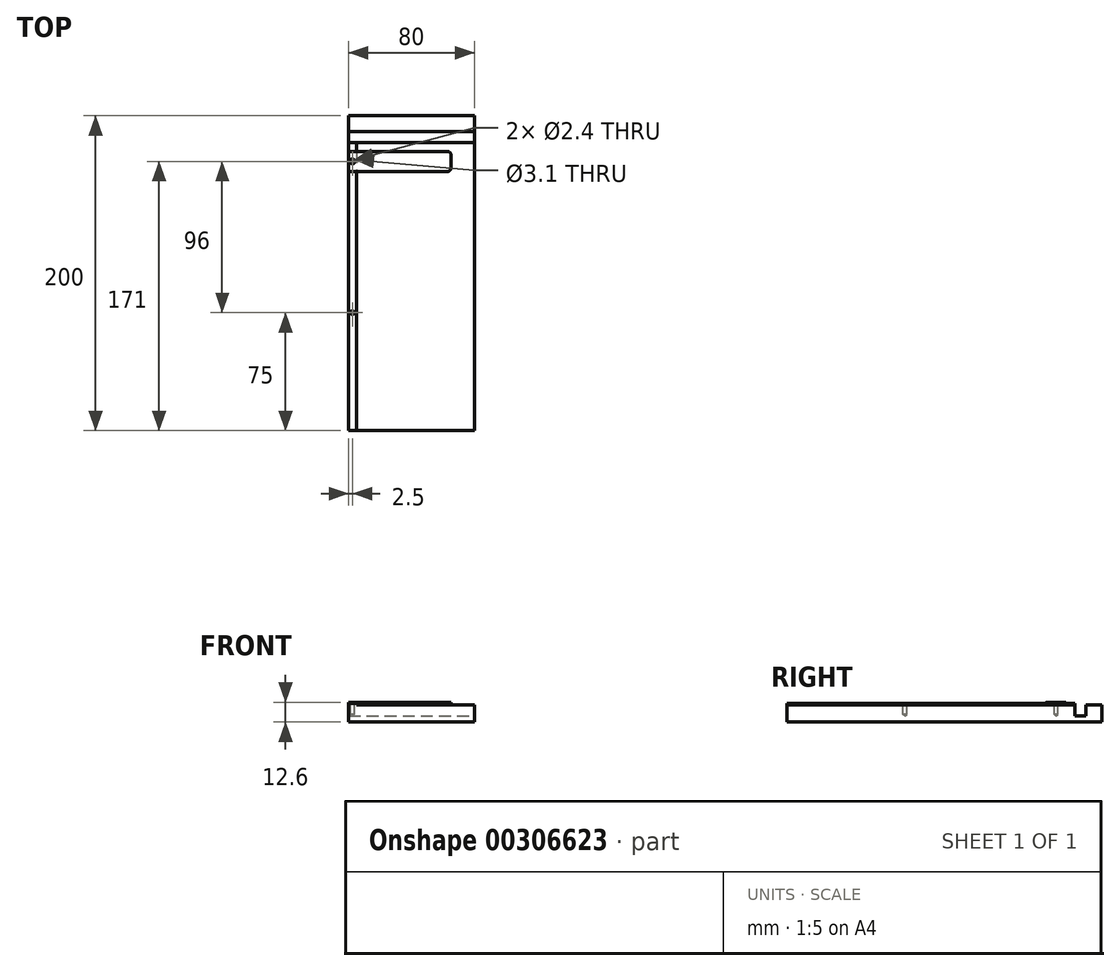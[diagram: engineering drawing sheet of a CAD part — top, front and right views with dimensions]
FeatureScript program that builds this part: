
annotation { "Feature Type Name" : "Feature", "Feature Type Description" : "" }
export const myFeature = defineFeature(function(context is Context, id is Id, definition is map)
    precondition{}
    {
        {
            var Q0;
            Q0=qCreatedBy(makeId("Right.planeOp"),FACE);
            var sketch = newSketch(context, id + "F0", { "sketchPlane" : qUnion([Q0])});
            skLineSegment(sketch, "E0", {"start": v(0, 0) * mm, "end": v(183, 0) * mm});
            skLineSegment(sketch, "E1", {"start": v(183, 0) * mm, "end": v(183, -7) * mm});
            skLineSegment(sketch, "E2", {"start": v(183, -7) * mm, "end": v(190, -7) * mm});
            skLineSegment(sketch, "E3", {"start": v(190, -7) * mm, "end": v(190, 0) * mm});
            skLineSegment(sketch, "E4", {"start": v(190, 0) * mm, "end": v(200, 0) * mm});
            skLineSegment(sketch, "E5", {"start": v(200, 0) * mm, "end": v(200, -11) * mm});
            skLineSegment(sketch, "E6", {"start": v(200, -11) * mm, "end": v(0, -11) * mm});
            skLineSegment(sketch, "E7", {"start": v(0, -11) * mm, "end": v(0, 0) * mm});
            skSolve(sketch);
        }
        {
            var Q0;
            Q0=qSketchRegion(id+"F0",true);
            extrude(context, id + "F1", {"entities" : qUnion([Q0]), "oppositeDirection" : true, "depth" : 80 * mm});
        }
        {
            var Q0;
            Q0=makeQuery(id+"F1.opExtrude","SWEPT_FACE",FACE,{"disambiguationData":[OSD([sQuery(id+"F0.wireOp",EDGE,"E0")])]});
            var sketch = newSketch(context, id + "F2", { "sketchPlane" : qUnion([Q0])});
            skLineSegment(sketch, "E8.bottom", {"start": v(-80, 183) * mm, "end": v(-75, 183) * mm});
            skLineSegment(sketch, "E8.top", {"start": v(-80, 0) * mm, "end": v(-75, 0) * mm});
            skLineSegment(sketch, "E8.left", {"start": v(-80, 183) * mm, "end": v(-80, 0) * mm});
            skLineSegment(sketch, "E8.right", {"start": v(-75, 183) * mm, "end": v(-75, 0) * mm});
            skSolve(sketch);
        }
        {
            var Q0;
            Q0=qSketchRegion(id+"F2",true);
            extrude(context, id + "F3", {"entities" : qUnion([Q0]), "operationType" : NewBodyOperationType.ADD, "depth" : 1 * mm});
        }
        {
            var Q0;
            Q0=makeQuery(id+"F3.opExtrude","CAP_FACE",FACE,{"disambiguationData":[OSD([sQuery(id+"F2.wireOp",EDGE,"E8.bottom"),sQuery(id+"F2.wireOp",EDGE,"E8.top"),sQuery(id+"F2.wireOp",EDGE,"E8.left"),sQuery(id+"F2.wireOp",EDGE,"E8.right")])],"isStart":false});
            var sketch = newSketch(context, id + "F4", { "sketchPlane" : qUnion([Q0])});
            skPoint(sketch, "E9", {"position": v(-77.5, 171) * mm});
            skPoint(sketch, "E10", {"position": v(-77.5, 75) * mm});
            skSolve(sketch);
        }
        {
            var Q0;
            Q0=sQuery(id+"F4.wireOp",VERTEX,"E9");
            var Q1;
            Q1=sQuery(id+"F4.wireOp",VERTEX,"E10");
            var Q2;
            Q2=makeQuery(id+"F1.opExtrude","SWEPT_BODY",BODY,{"disambiguationData":[OSD([sQuery(id+"F0.wireOp",EDGE,"E0"),sQuery(id+"F0.wireOp",EDGE,"E1"),sQuery(id+"F0.wireOp",EDGE,"E2"),sQuery(id+"F0.wireOp",EDGE,"E3"),sQuery(id+"F0.wireOp",EDGE,"E4"),sQuery(id+"F0.wireOp",EDGE,"E5"),sQuery(id+"F0.wireOp",EDGE,"E6"),sQuery(id+"F0.wireOp",EDGE,"E7")])]});
            hole(context, id + "F5", {"style" : HoleStyle.SIMPLE, "endStyle" : HoleEndStyle.BLIND, "standardTappedOrClearance" : lookupTablePath({ "standard" : "ISO", "engagement" : "75%", "pitch" : "0.6 mm", "size" : "M3", "type" : "Tapped" }), "standardBlindInLast" : lookupTablePath({ "standard" : "ISO", "engagement" : "75%", "pitch" : "0.6 mm", "size" : "M3", "type" : "Tapped" }), "holeDiameter" : 2.4 * mm, "showTappedDepth" : true, "holeDepth" : 7.2 * mm, "tappedDepth" : 6 * mm, "tapClearance" : 2, "locations" : qUnion([Q0, Q1]), "scope" : qUnion([Q2])});
        }
        {
            var Q0;
            Q0=makeQuery(id+"F3.opExtrude","CAP_FACE",FACE,{"disambiguationData":[OSD([sQuery(id+"F2.wireOp",EDGE,"E8.bottom"),sQuery(id+"F2.wireOp",EDGE,"E8.top"),sQuery(id+"F2.wireOp",EDGE,"E8.left"),sQuery(id+"F2.wireOp",EDGE,"E8.right")])],"isStart":false});
            var sketch = newSketch(context, id + "F6", { "sketchPlane" : qUnion([Q0])});
            skLineSegment(sketch, "E11.bottom", {"start": v(-80, 177.35) * mm, "end": v(-17, 177.35) * mm});
            skLineSegment(sketch, "E11.top", {"start": v(-80, 164.65) * mm, "end": v(-17, 164.65) * mm});
            skLineSegment(sketch, "E11.left", {"start": v(-80, 177.35) * mm, "end": v(-80, 164.65) * mm});
            skLineSegment(sketch, "E11.right", {"start": v(-15, 175.35) * mm, "end": v(-15, 166.65) * mm});
            skPoint(sketch, "E12", {"position": v(-80, 171) * mm});
            skCircle(sketch, "E13", {"center": v(-77.5, 171) * mm, "radius": 1.55 * mm});
            skPoint(sketch, "E14.visualSharp", {"position": v(-15, 177.35) * mm});
            skArc(sketch, "E14.filletArc", {"start": v(-15, 175.35) * mm, "mid": v(-15.59, 176.76) * mm, "end": v(-17, 177.35) * mm});
            skPoint(sketch, "E15.visualSharp", {"position": v(-15, 164.65) * mm});
            skArc(sketch, "E15.filletArc", {"start": v(-17, 164.65) * mm, "mid": v(-15.59, 165.24) * mm, "end": v(-15, 166.65) * mm});
            skSolve(sketch);
        }
        {
            var Q0;
            Q0=qSketchRegion(id+"F6",true);
            extrude(context, id + "F7", {"entities" : qUnion([Q0]), "flatOperationType" : FlatOperationType.REMOVE, "offsetDistance" : 25 * mm, "depth" : .6 * mm, "domain" : OperationDomain.MODEL});
        }
    });
